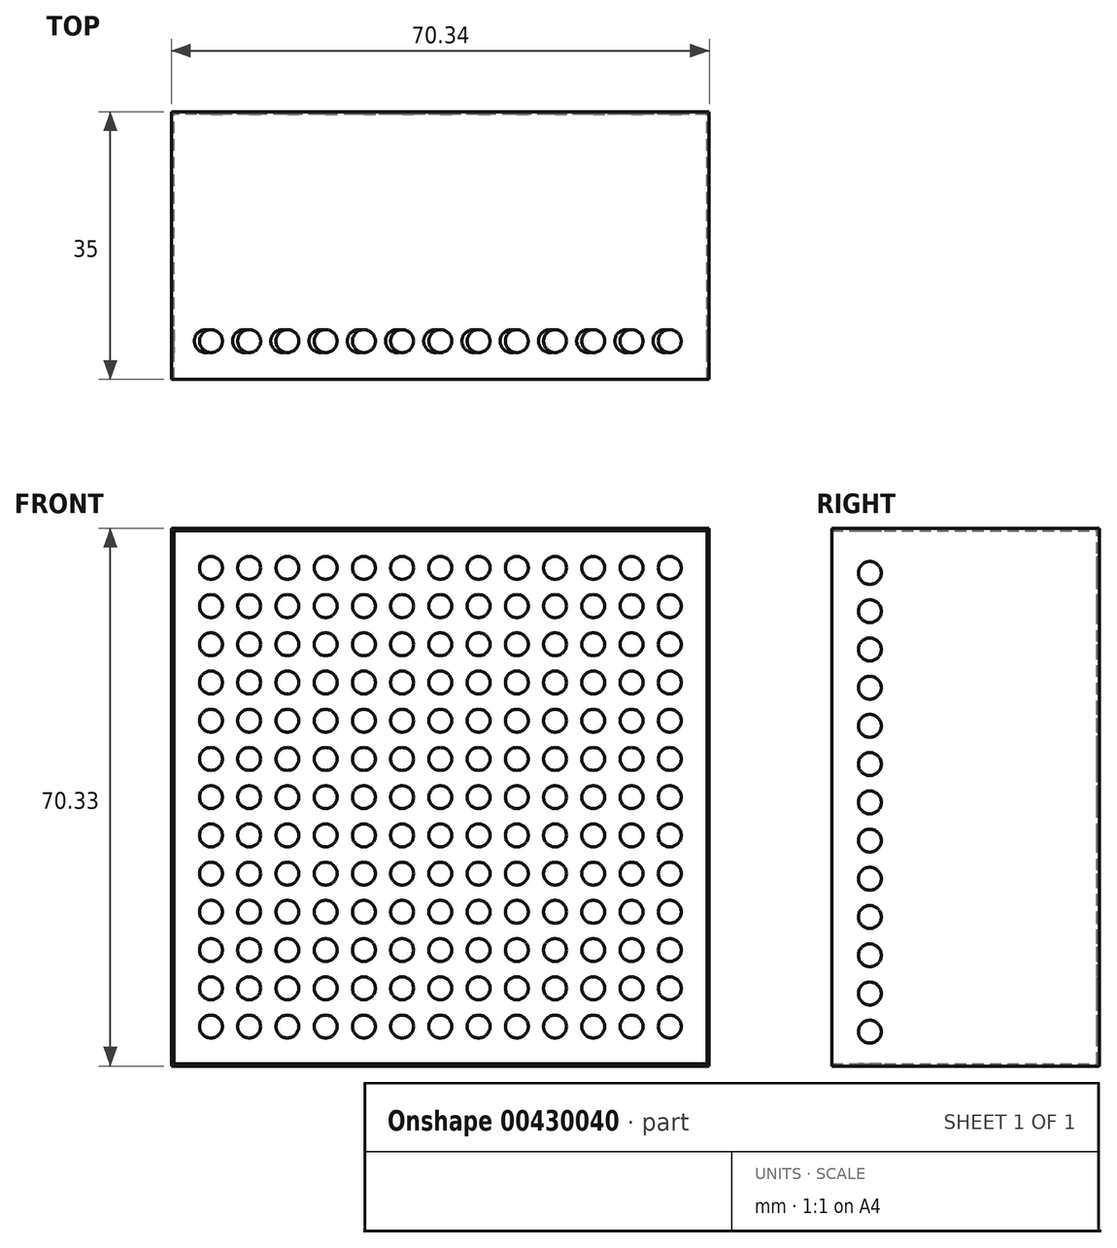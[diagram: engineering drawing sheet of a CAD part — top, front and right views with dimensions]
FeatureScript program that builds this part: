
annotation { "Feature Type Name" : "Feature", "Feature Type Description" : "" }
export const myFeature = defineFeature(function(context is Context, id is Id, definition is map)
    precondition{}
    {
        {
            var Q0;
            Q0=qCreatedBy(makeId("Front.planeOp"),FACE);
            var sketch = newSketch(context, id + "F0", { "sketchPlane" : qUnion([Q0])});
            skLineSegment(sketch, "E0.bottom", {"start": v(35.16, -35.16) * mm, "end": v(-35.16, -35.17) * mm});
            skLineSegment(sketch, "E0.top", {"start": v(35.16, 35.16) * mm, "end": v(-35.16, 35.16) * mm});
            skLineSegment(sketch, "E0.left", {"start": v(35.16, -35.16) * mm, "end": v(35.16, 35.16) * mm});
            skLineSegment(sketch, "E0.right", {"start": v(-35.16, -35.17) * mm, "end": v(-35.16, 35.16) * mm});
            skPoint(sketch, "E0.middle", {"position": v(0, 0) * mm});
            skLineSegment(sketch, "E1", {"start": v(0, 50.16) * mm, "end": v(0, -40.93) * mm, "construction": true});
            skPoint(sketch, "E1.endSnap0", {"position": v(0, 35.16) * mm});
            skLineSegment(sketch, "E2", {"start": v(-54.3, 0) * mm, "end": v(79.67, 0) * mm, "construction": true});
            skPoint(sketch, "E3", {"position": v(-30, 30) * mm});
            skPoint(sketch, "E4.1.0.0", {"position": v(-25, 30) * mm});
            skPoint(sketch, "E4.2.0.0", {"position": v(-20, 30) * mm});
            skPoint(sketch, "E4.3.0.0", {"position": v(-15, 30) * mm});
            skPoint(sketch, "E4.4.0.0", {"position": v(-10, 30) * mm});
            skPoint(sketch, "E4.5.0.0", {"position": v(-5, 30) * mm});
            skPoint(sketch, "E4.6.0.0", {"position": v(0, 30) * mm});
            skPoint(sketch, "E4.7.0.0", {"position": v(5, 30) * mm});
            skPoint(sketch, "E4.8.0.0", {"position": v(10, 30) * mm});
            skPoint(sketch, "E4.9.0.0", {"position": v(15, 30) * mm});
            skPoint(sketch, "E4.10.0.0", {"position": v(20, 30) * mm});
            skPoint(sketch, "E4.11.0.0", {"position": v(25, 30) * mm});
            skPoint(sketch, "E4.12.0.0", {"position": v(30, 30) * mm});
            skLineSegment(sketch, "E4.direction1", {"start": v(-30, 30) * mm, "end": v(-25, 30) * mm, "construction": true});
            skLineSegment(sketch, "E5", {"start": v(-44.02, 27.5) * mm, "end": v(49.73, 27.5) * mm, "construction": true});
            skLineSegment(sketch, "E6", {"start": v(-45.28, 22.5) * mm, "end": v(51.67, 22.5) * mm, "construction": true});
            skLineSegment(sketch, "E7", {"start": v(-45.19, 17.5) * mm, "end": v(53.22, 17.5) * mm, "construction": true});
            skPoint(sketch, "E8.MirrorP", {"position": v(-30, 25) * mm});
            skPoint(sketch, "E9.MirrorP", {"position": v(-25, 25) * mm});
            skPoint(sketch, "E10.MirrorP", {"position": v(-20, 25) * mm});
            skPoint(sketch, "E11.MirrorP", {"position": v(-15, 25) * mm});
            skPoint(sketch, "E12.MirrorP", {"position": v(-10, 25) * mm});
            skPoint(sketch, "E13.MirrorP", {"position": v(-5, 25) * mm});
            skPoint(sketch, "E14.MirrorP", {"position": v(0, 25) * mm});
            skPoint(sketch, "E15.MirrorP", {"position": v(5, 25) * mm});
            skPoint(sketch, "E16.MirrorP", {"position": v(10, 25) * mm});
            skPoint(sketch, "E17.MirrorP", {"position": v(15, 25) * mm});
            skPoint(sketch, "E18.MirrorP", {"position": v(20, 25) * mm});
            skPoint(sketch, "E19.MirrorP", {"position": v(25, 25) * mm});
            skPoint(sketch, "E20.MirrorP", {"position": v(30, 25) * mm});
            skPoint(sketch, "E21.MirrorP", {"position": v(-30, 20) * mm});
            skPoint(sketch, "E22.MirrorP", {"position": v(-25, 20) * mm});
            skPoint(sketch, "E23.MirrorP", {"position": v(-20, 20) * mm});
            skPoint(sketch, "E24.MirrorP", {"position": v(-15, 20) * mm});
            skPoint(sketch, "E25.MirrorP", {"position": v(-10, 20) * mm});
            skPoint(sketch, "E26.MirrorP", {"position": v(-5, 20) * mm});
            skPoint(sketch, "E27.MirrorP", {"position": v(0, 20) * mm});
            skPoint(sketch, "E28.MirrorP", {"position": v(5, 20) * mm});
            skPoint(sketch, "E29.MirrorP", {"position": v(10, 20) * mm});
            skPoint(sketch, "E30.MirrorP", {"position": v(15, 20) * mm});
            skPoint(sketch, "E31.MirrorP", {"position": v(20, 20) * mm});
            skPoint(sketch, "E32.MirrorP", {"position": v(25, 20) * mm});
            skPoint(sketch, "E33.MirrorP", {"position": v(30, 20) * mm});
            skPoint(sketch, "E34.MirrorP", {"position": v(-30, 15) * mm});
            skPoint(sketch, "E35.MirrorP", {"position": v(-25, 15) * mm});
            skPoint(sketch, "E36.MirrorP", {"position": v(-20, 15) * mm});
            skPoint(sketch, "E37.MirrorP", {"position": v(-15, 15) * mm});
            skPoint(sketch, "E38.MirrorP", {"position": v(-10, 15) * mm});
            skPoint(sketch, "E39.MirrorP", {"position": v(-5, 15) * mm});
            skPoint(sketch, "E40.MirrorP", {"position": v(0, 15) * mm});
            skPoint(sketch, "E41.MirrorP", {"position": v(10, 15) * mm});
            skPoint(sketch, "E42.MirrorP", {"position": v(20, 15) * mm});
            skPoint(sketch, "E43.MirrorP", {"position": v(5, 15) * mm});
            skPoint(sketch, "E44.MirrorP", {"position": v(25, 15) * mm});
            skPoint(sketch, "E45.MirrorP", {"position": v(15, 15) * mm});
            skPoint(sketch, "E46.MirrorP", {"position": v(30, 15) * mm});
            skLineSegment(sketch, "E47", {"start": v(-45.96, 12.5) * mm, "end": v(53.42, 12.5) * mm, "construction": true});
            skLineSegment(sketch, "E48", {"start": v(-45.28, 7.5) * mm, "end": v(54.1, 7.5) * mm, "construction": true});
            skLineSegment(sketch, "E49", {"start": v(-42.28, 2.5) * mm, "end": v(50.9, 2.5) * mm, "construction": true});
            skPoint(sketch, "E50.MirrorP", {"position": v(-30, 10) * mm});
            skPoint(sketch, "E51.MirrorP", {"position": v(-25, 10) * mm});
            skPoint(sketch, "E52.MirrorP", {"position": v(-20, 10) * mm});
            skPoint(sketch, "E53.MirrorP", {"position": v(-15, 10) * mm});
            skPoint(sketch, "E54.MirrorP", {"position": v(-10, 10) * mm});
            skPoint(sketch, "E55.MirrorP", {"position": v(-5, 10) * mm});
            skPoint(sketch, "E56.MirrorP", {"position": v(0, 10) * mm});
            skPoint(sketch, "E57.MirrorP", {"position": v(5, 10) * mm});
            skPoint(sketch, "E58.MirrorP", {"position": v(10, 10) * mm});
            skPoint(sketch, "E59.MirrorP", {"position": v(15, 10) * mm});
            skPoint(sketch, "E60.MirrorP", {"position": v(20, 10) * mm});
            skPoint(sketch, "E61.MirrorP", {"position": v(30, 10) * mm});
            skPoint(sketch, "E62.MirrorP", {"position": v(25, 10) * mm});
            skPoint(sketch, "E63.MirrorP", {"position": v(-30, 5) * mm});
            skPoint(sketch, "E64.MirrorP", {"position": v(-25, 5) * mm});
            skPoint(sketch, "E65.MirrorP", {"position": v(15, 5) * mm});
            skPoint(sketch, "E66.MirrorP", {"position": v(-15, 5) * mm});
            skPoint(sketch, "E67.MirrorP", {"position": v(-20, 5) * mm});
            skPoint(sketch, "E68.MirrorP", {"position": v(30, 5) * mm});
            skPoint(sketch, "E69.MirrorP", {"position": v(-5, 5) * mm});
            skPoint(sketch, "E70.MirrorP", {"position": v(20, 5) * mm});
            skPoint(sketch, "E71.MirrorP", {"position": v(-10, 5) * mm});
            skPoint(sketch, "E72.MirrorP", {"position": v(10, 5) * mm});
            skPoint(sketch, "E73.MirrorP", {"position": v(5, 5) * mm});
            skPoint(sketch, "E74.MirrorP", {"position": v(25, 5) * mm});
            skPoint(sketch, "E75.MirrorP", {"position": v(0, 5) * mm});
            skPoint(sketch, "E76.MirrorP", {"position": v(30, 0) * mm});
            skPoint(sketch, "E77.MirrorP", {"position": v(5, 0) * mm});
            skPoint(sketch, "E78.MirrorP", {"position": v(10, 0) * mm});
            skPoint(sketch, "E79.MirrorP", {"position": v(15, 0) * mm});
            skPoint(sketch, "E80.MirrorP", {"position": v(-5, 0) * mm});
            skPoint(sketch, "E81.MirrorP", {"position": v(-10, 0) * mm});
            skPoint(sketch, "E82.MirrorP", {"position": v(-25, 0) * mm});
            skPoint(sketch, "E83.MirrorP", {"position": v(-15, 0) * mm});
            skPoint(sketch, "E84.MirrorP", {"position": v(20, 0) * mm});
            skPoint(sketch, "E85.MirrorP", {"position": v(-20, 0) * mm});
            skPoint(sketch, "E86.MirrorP", {"position": v(-30, 0) * mm});
            skPoint(sketch, "E87.MirrorP", {"position": v(25, 0) * mm});
            skPoint(sketch, "E88.MirrorP", {"position": v(-15, -20) * mm});
            skPoint(sketch, "E89.MirrorP", {"position": v(0, -15) * mm});
            skPoint(sketch, "E90.MirrorP", {"position": v(15, -10) * mm});
            skPoint(sketch, "E91.MirrorP", {"position": v(0, -5) * mm});
            skPoint(sketch, "E92.MirrorP", {"position": v(-30, -25) * mm});
            skPoint(sketch, "E93.MirrorP", {"position": v(-20, -10) * mm});
            skPoint(sketch, "E94.MirrorP", {"position": v(30, -5) * mm});
            skPoint(sketch, "E95.MirrorP", {"position": v(0, -30) * mm});
            skPoint(sketch, "E96.MirrorP", {"position": v(15, -25) * mm});
            skPoint(sketch, "E97.MirrorP", {"position": v(30, -20) * mm});
            skPoint(sketch, "E98.MirrorP", {"position": v(-30, -15) * mm});
            skPoint(sketch, "E99.MirrorP", {"position": v(20, -25) * mm});
            skPoint(sketch, "E100.MirrorP", {"position": v(5, -30) * mm});
            skPoint(sketch, "E101.MirrorP", {"position": v(-5, -5) * mm});
            skPoint(sketch, "E102.MirrorP", {"position": v(-15, -10) * mm});
            skPoint(sketch, "E103.MirrorP", {"position": v(-25, -25) * mm});
            skPoint(sketch, "E104.MirrorP", {"position": v(20, -10) * mm});
            skPoint(sketch, "E105.MirrorP", {"position": v(0, -10) * mm});
            skPoint(sketch, "E106.MirrorP", {"position": v(30, -15) * mm});
            skPoint(sketch, "E107.MirrorP", {"position": v(10, -15) * mm});
            skPoint(sketch, "E108.MirrorP", {"position": v(10, -5) * mm});
            skPoint(sketch, "E109.MirrorP", {"position": v(-10, -20) * mm});
            skPoint(sketch, "E110.MirrorP", {"position": v(15, -5) * mm});
            skPoint(sketch, "E111.MirrorP", {"position": v(-15, -5) * mm});
            skPoint(sketch, "E112.MirrorP", {"position": v(-30, -10) * mm});
            skPoint(sketch, "E113.MirrorP", {"position": v(20, -30) * mm});
            skPoint(sketch, "E114.MirrorP", {"position": v(-20, -25) * mm});
            skLineSegment(sketch, "E115.MirrorCS", {"start": v(-30, -30) * mm, "end": v(-25, -30) * mm, "construction": true});
            skPoint(sketch, "E116.MirrorP", {"position": v(30, -10) * mm});
            skPoint(sketch, "E117.MirrorP", {"position": v(-10, -30) * mm});
            skPoint(sketch, "E118.MirrorP", {"position": v(5, -25) * mm});
            skPoint(sketch, "E119.MirrorP", {"position": v(20, -15) * mm});
            skPoint(sketch, "E120.MirrorP", {"position": v(-5, -20) * mm});
            skPoint(sketch, "E121.MirrorP", {"position": v(15, -15) * mm});
            skPoint(sketch, "E122.MirrorP", {"position": v(-25, -5) * mm});
            skPoint(sketch, "E123.MirrorP", {"position": v(25, -25) * mm});
            skPoint(sketch, "E124.MirrorP", {"position": v(-25, -30) * mm});
            skPoint(sketch, "E125.MirrorP", {"position": v(5, -15) * mm});
            skPoint(sketch, "E126.MirrorP", {"position": v(-15, -25) * mm});
            skPoint(sketch, "E127.MirrorP", {"position": v(30, -25) * mm});
            skPoint(sketch, "E128.MirrorP", {"position": v(15, -30) * mm});
            skPoint(sketch, "E129.MirrorP", {"position": v(-25, -10) * mm});
            skPoint(sketch, "E130.MirrorP", {"position": v(-5, -10) * mm});
            skPoint(sketch, "E131.MirrorP", {"position": v(25, -15) * mm});
            skPoint(sketch, "E132.MirrorP", {"position": v(-10, -10) * mm});
            skPoint(sketch, "E133.MirrorP", {"position": v(30, -30) * mm});
            skPoint(sketch, "E134.MirrorP", {"position": v(-30, -30) * mm});
            skPoint(sketch, "E135.MirrorP", {"position": v(-10, -5) * mm});
            skPoint(sketch, "E136.MirrorP", {"position": v(20, -5) * mm});
            skPoint(sketch, "E137.MirrorP", {"position": v(0, -20) * mm});
            skPoint(sketch, "E138.MirrorP", {"position": v(-20, -20) * mm});
            skPoint(sketch, "E139.MirrorP", {"position": v(20, -20) * mm});
            skPoint(sketch, "E140.MirrorP", {"position": v(5, -10) * mm});
            skPoint(sketch, "E141.MirrorP", {"position": v(25, -30) * mm});
            skPoint(sketch, "E142.MirrorP", {"position": v(5, -5) * mm});
            skPoint(sketch, "E143.MirrorP", {"position": v(10, -30) * mm});
            skPoint(sketch, "E144.MirrorP", {"position": v(25, -5) * mm});
            skPoint(sketch, "E145.MirrorP", {"position": v(-20, -30) * mm});
            skPoint(sketch, "E146.MirrorP", {"position": v(25, -10) * mm});
            skPoint(sketch, "E147.MirrorP", {"position": v(15, -20) * mm});
            skPoint(sketch, "E148.MirrorP", {"position": v(-5, -25) * mm});
            skPoint(sketch, "E149.MirrorP", {"position": v(10, -25) * mm});
            skPoint(sketch, "E150.MirrorP", {"position": v(10, -10) * mm});
            skPoint(sketch, "E151.MirrorP", {"position": v(-30, -5) * mm});
            skPoint(sketch, "E152.MirrorP", {"position": v(-5, -15) * mm});
            skPoint(sketch, "E153.MirrorP", {"position": v(-10, -15) * mm});
            skPoint(sketch, "E154.MirrorP", {"position": v(10, -20) * mm});
            skPoint(sketch, "E155.MirrorP", {"position": v(-20, -5) * mm});
            skPoint(sketch, "E156.MirrorP", {"position": v(-5, -30) * mm});
            skPoint(sketch, "E157.MirrorP", {"position": v(5, -20) * mm});
            skPoint(sketch, "E158.MirrorP", {"position": v(-25, -15) * mm});
            skPoint(sketch, "E159.MirrorP", {"position": v(-30, -20) * mm});
            skPoint(sketch, "E160.MirrorP", {"position": v(-15, -30) * mm});
            skPoint(sketch, "E161.MirrorP", {"position": v(25, -20) * mm});
            skPoint(sketch, "E162.MirrorP", {"position": v(-10, -25) * mm});
            skPoint(sketch, "E163.MirrorP", {"position": v(-15, -15) * mm});
            skPoint(sketch, "E164.MirrorP", {"position": v(-20, -15) * mm});
            skPoint(sketch, "E165.MirrorP", {"position": v(0, -25) * mm});
            skPoint(sketch, "E166.MirrorP", {"position": v(-25, -20) * mm});
            skSolve(sketch);
        }
        {
            var Q0;
            Q0=makeQuery(id+"F0.imprint","IMPRINT",FACE,{"disambiguationData":[TD([[makeQuery(id+"F0.imprint","IMPRINT",EDGE,{"derivedFrom":sQuery(id+"F0.wireOp",EDGE,"E0.bottom")}),-1.0]])]});
            extrude(context, id + "F1", {"entities" : qUnion([Q0]), "depth" : 35 * mm});
        }
        {
            var Q0;
            Q0=makeQuery(id+"F1.opExtrude","CAP_FACE",FACE,{"disambiguationData":[OSD([sQuery(id+"F0.wireOp",EDGE,"E0.bottom"),sQuery(id+"F0.wireOp",EDGE,"E0.top"),sQuery(id+"F0.wireOp",EDGE,"E0.left"),sQuery(id+"F0.wireOp",EDGE,"E0.right")])],"isStart":false});
            shell(context, id + "F2", {"entities" : qUnion([Q0]), "thickness" : 0.3 * mm});
        }
        {
            var Q0;
            Q0=sQuery(id+"F0.wireOp",VERTEX,"E4.12.0.0");
            var Q1;
            Q1=sQuery(id+"F0.wireOp",VERTEX,"E42.MirrorP");
            var Q2;
            Q2=sQuery(id+"F0.wireOp",VERTEX,"E29.MirrorP");
            var Q3;
            Q3=sQuery(id+"F0.wireOp",VERTEX,"E17.MirrorP");
            var Q4;
            Q4=sQuery(id+"F0.wireOp",VERTEX,"E30.MirrorP");
            var Q5;
            Q5=sQuery(id+"F0.wireOp",VERTEX,"E4.9.0.0");
            var Q6;
            Q6=sQuery(id+"F0.wireOp",VERTEX,"E4.7.0.0");
            var Q7;
            Q7=sQuery(id+"F0.wireOp",VERTEX,"E43.MirrorP");
            var Q8;
            Q8=sQuery(id+"F0.wireOp",VERTEX,"E18.MirrorP");
            var Q9;
            Q9=sQuery(id+"F0.wireOp",VERTEX,"E41.MirrorP");
            var Q10;
            Q10=sQuery(id+"F0.wireOp",VERTEX,"E4.10.0.0");
            var Q11;
            Q11=sQuery(id+"F0.wireOp",VERTEX,"E45.MirrorP");
            var Q12;
            Q12=sQuery(id+"F0.wireOp",VERTEX,"E16.MirrorP");
            var Q13;
            Q13=sQuery(id+"F0.wireOp",VERTEX,"E32.MirrorP");
            var Q14;
            Q14=sQuery(id+"F0.wireOp",VERTEX,"E28.MirrorP");
            var Q15;
            Q15=sQuery(id+"F0.wireOp",VERTEX,"E19.MirrorP");
            var Q16;
            Q16=sQuery(id+"F0.wireOp",VERTEX,"E4.8.0.0");
            var Q17;
            Q17=sQuery(id+"F0.wireOp",VERTEX,"E44.MirrorP");
            var Q18;
            Q18=sQuery(id+"F0.wireOp",VERTEX,"E31.MirrorP");
            var Q19;
            Q19=sQuery(id+"F0.wireOp",VERTEX,"E15.MirrorP");
            var Q20;
            Q20=sQuery(id+"F0.wireOp",VERTEX,"E4.11.0.0");
            var Q21;
            Q21=sQuery(id+"F0.wireOp",VERTEX,"E33.MirrorP");
            var Q22;
            Q22=sQuery(id+"F0.wireOp",VERTEX,"E46.MirrorP");
            var Q23;
            Q23=sQuery(id+"F0.wireOp",VERTEX,"E68.MirrorP");
            var Q24;
            Q24=sQuery(id+"F0.wireOp",VERTEX,"E61.MirrorP");
            var Q25;
            Q25=sQuery(id+"F0.wireOp",VERTEX,"E76.MirrorP");
            var Q26;
            Q26=sQuery(id+"F0.wireOp",VERTEX,"E20.MirrorP");
            var Q27;
            Q27=sQuery(id+"F0.wireOp",VERTEX,"E106.MirrorP");
            var Q28;
            Q28=sQuery(id+"F0.wireOp",VERTEX,"E116.MirrorP");
            var Q29;
            Q29=sQuery(id+"F0.wireOp",VERTEX,"E94.MirrorP");
            var Q30;
            Q30=sQuery(id+"F0.wireOp",VERTEX,"E127.MirrorP");
            var Q31;
            Q31=sQuery(id+"F0.wireOp",VERTEX,"E97.MirrorP");
            var Q32;
            Q32=sQuery(id+"F0.wireOp",VERTEX,"E149.MirrorP");
            var Q33;
            Q33=sQuery(id+"F0.wireOp",VERTEX,"E96.MirrorP");
            var Q34;
            Q34=sQuery(id+"F0.wireOp",VERTEX,"E142.MirrorP");
            var Q35;
            Q35=sQuery(id+"F0.wireOp",VERTEX,"E157.MirrorP");
            var Q36;
            Q36=sQuery(id+"F0.wireOp",VERTEX,"E62.MirrorP");
            var Q37;
            Q37=sQuery(id+"F0.wireOp",VERTEX,"E74.MirrorP");
            var Q38;
            Q38=sQuery(id+"F0.wireOp",VERTEX,"E131.MirrorP");
            var Q39;
            Q39=sQuery(id+"F0.wireOp",VERTEX,"E161.MirrorP");
            var Q40;
            Q40=sQuery(id+"F0.wireOp",VERTEX,"E147.MirrorP");
            var Q41;
            Q41=sQuery(id+"F0.wireOp",VERTEX,"E65.MirrorP");
            var Q42;
            Q42=sQuery(id+"F0.wireOp",VERTEX,"E77.MirrorP");
            var Q43;
            Q43=sQuery(id+"F0.wireOp",VERTEX,"E100.MirrorP");
            var Q44;
            Q44=sQuery(id+"F0.wireOp",VERTEX,"E99.MirrorP");
            var Q45;
            Q45=sQuery(id+"F0.wireOp",VERTEX,"E84.MirrorP");
            var Q46;
            Q46=sQuery(id+"F0.wireOp",VERTEX,"E90.MirrorP");
            var Q47;
            Q47=sQuery(id+"F0.wireOp",VERTEX,"E139.MirrorP");
            var Q48;
            Q48=sQuery(id+"F0.wireOp",VERTEX,"E123.MirrorP");
            var Q49;
            Q49=sQuery(id+"F0.wireOp",VERTEX,"E60.MirrorP");
            var Q50;
            Q50=sQuery(id+"F0.wireOp",VERTEX,"E140.MirrorP");
            var Q51;
            Q51=sQuery(id+"F0.wireOp",VERTEX,"E107.MirrorP");
            var Q52;
            Q52=sQuery(id+"F0.wireOp",VERTEX,"E72.MirrorP");
            var Q53;
            Q53=sQuery(id+"F0.wireOp",VERTEX,"E59.MirrorP");
            var Q54;
            Q54=sQuery(id+"F0.wireOp",VERTEX,"E128.MirrorP");
            var Q55;
            Q55=sQuery(id+"F0.wireOp",VERTEX,"E144.MirrorP");
            var Q56;
            Q56=sQuery(id+"F0.wireOp",VERTEX,"E79.MirrorP");
            var Q57;
            Q57=sQuery(id+"F0.wireOp",VERTEX,"E119.MirrorP");
            var Q58;
            Q58=sQuery(id+"F0.wireOp",VERTEX,"E108.MirrorP");
            var Q59;
            Q59=sQuery(id+"F0.wireOp",VERTEX,"E125.MirrorP");
            var Q60;
            Q60=sQuery(id+"F0.wireOp",VERTEX,"E141.MirrorP");
            var Q61;
            Q61=sQuery(id+"F0.wireOp",VERTEX,"E154.MirrorP");
            var Q62;
            Q62=sQuery(id+"F0.wireOp",VERTEX,"E58.MirrorP");
            var Q63;
            Q63=sQuery(id+"F0.wireOp",VERTEX,"E136.MirrorP");
            var Q64;
            Q64=sQuery(id+"F0.wireOp",VERTEX,"E87.MirrorP");
            var Q65;
            Q65=sQuery(id+"F0.wireOp",VERTEX,"E78.MirrorP");
            var Q66;
            Q66=sQuery(id+"F0.wireOp",VERTEX,"E70.MirrorP");
            var Q67;
            Q67=sQuery(id+"F0.wireOp",VERTEX,"E143.MirrorP");
            var Q68;
            Q68=sQuery(id+"F0.wireOp",VERTEX,"E150.MirrorP");
            var Q69;
            Q69=sQuery(id+"F0.wireOp",VERTEX,"E118.MirrorP");
            var Q70;
            Q70=sQuery(id+"F0.wireOp",VERTEX,"E110.MirrorP");
            var Q71;
            Q71=sQuery(id+"F0.wireOp",VERTEX,"E146.MirrorP");
            var Q72;
            Q72=sQuery(id+"F0.wireOp",VERTEX,"E113.MirrorP");
            var Q73;
            Q73=sQuery(id+"F0.wireOp",VERTEX,"E73.MirrorP");
            var Q74;
            Q74=sQuery(id+"F0.wireOp",VERTEX,"E57.MirrorP");
            var Q75;
            Q75=sQuery(id+"F0.wireOp",VERTEX,"E121.MirrorP");
            var Q76;
            Q76=sQuery(id+"F0.wireOp",VERTEX,"E104.MirrorP");
            var Q77;
            Q77=sQuery(id+"F0.wireOp",VERTEX,"E89.MirrorP");
            var Q78;
            Q78=sQuery(id+"F0.wireOp",VERTEX,"E133.MirrorP");
            var Q79;
            Q79=sQuery(id+"F0.wireOp",VERTEX,"E158.MirrorP");
            var Q80;
            Q80=sQuery(id+"F0.wireOp",VERTEX,"E164.MirrorP");
            var Q81;
            Q81=sQuery(id+"F0.wireOp",VERTEX,"E152.MirrorP");
            var Q82;
            Q82=sQuery(id+"F0.wireOp",VERTEX,"E98.MirrorP");
            var Q83;
            Q83=sQuery(id+"F0.wireOp",VERTEX,"E163.MirrorP");
            var Q84;
            Q84=sQuery(id+"F0.wireOp",VERTEX,"E153.MirrorP");
            var Q85;
            Q85=sQuery(id+"F0.wireOp",VERTEX,"E109.MirrorP");
            var Q86;
            Q86=sQuery(id+"F0.wireOp",VERTEX,"E138.MirrorP");
            var Q87;
            Q87=sQuery(id+"F0.wireOp",VERTEX,"E120.MirrorP");
            var Q88;
            Q88=sQuery(id+"F0.wireOp",VERTEX,"E166.MirrorP");
            var Q89;
            Q89=sQuery(id+"F0.wireOp",VERTEX,"E159.MirrorP");
            var Q90;
            Q90=sQuery(id+"F0.wireOp",VERTEX,"E137.MirrorP");
            var Q91;
            Q91=sQuery(id+"F0.wireOp",VERTEX,"E88.MirrorP");
            var Q92;
            Q92=sQuery(id+"F0.wireOp",VERTEX,"E165.MirrorP");
            var Q93;
            Q93=sQuery(id+"F0.wireOp",VERTEX,"E114.MirrorP");
            var Q94;
            Q94=sQuery(id+"F0.wireOp",VERTEX,"E126.MirrorP");
            var Q95;
            Q95=sQuery(id+"F0.wireOp",VERTEX,"E92.MirrorP");
            var Q96;
            Q96=sQuery(id+"F0.wireOp",VERTEX,"E148.MirrorP");
            var Q97;
            Q97=sQuery(id+"F0.wireOp",VERTEX,"E103.MirrorP");
            var Q98;
            Q98=sQuery(id+"F0.wireOp",VERTEX,"E162.MirrorP");
            var Q99;
            Q99=makeQuery(id+"F1.opExtrude","SWEPT_BODY",BODY,{"disambiguationData":[OSD([sQuery(id+"F0.wireOp",EDGE,"E0.bottom"),sQuery(id+"F0.wireOp",EDGE,"E0.top"),sQuery(id+"F0.wireOp",EDGE,"E0.left"),sQuery(id+"F0.wireOp",EDGE,"E0.right")])]});
            hole(context, id + "F3", {"style" : HoleStyle.SIMPLE, "endStyle" : HoleEndStyle.BLIND, "oppositeDirection" : true, "holeDiameter" : 3 * mm, "holeDepth" : 1 * mm, "tappedDepth" : 12 * mm, "tapClearance" : 3, "locations" : qUnion([Q0, Q1, Q2, Q3, Q4, Q5, Q6, Q7, Q8, Q9, Q10, Q11, Q12, Q13, Q14, Q15, Q16, Q17, Q18, Q19, Q20, Q21, Q22, Q23, Q24, Q25, Q26, Q27, Q28, Q29, Q30, Q31, Q32, Q33, Q34, Q35, Q36, Q37, Q38, Q39, Q40, Q41, Q42, Q43, Q44, Q45, Q46, Q47, Q48, Q49, Q50, Q51, Q52, Q53, Q54, Q55, Q56, Q57, Q58, Q59, Q60, Q61, Q62, Q63, Q64, Q65, Q66, Q67, Q68, Q69, Q70, Q71, Q72, Q73, Q74, Q75, Q76, Q77, Q78, Q79, Q80, Q81, Q82, Q83, Q84, Q85, Q86, Q87, Q88, Q89, Q90, Q91, Q92, Q93, Q94, Q95, Q96, Q97, Q98]), "scope" : qUnion([Q99])});
        }
        {
            var Q0;
            Q0=sQuery(id+"F0.wireOp",VERTEX,"E4.3.0.0");
            var Q1;
            Q1=sQuery(id+"F0.wireOp",VERTEX,"E4.2.0.0");
            var Q2;
            Q2=sQuery(id+"F0.wireOp",VERTEX,"E4.6.0.0");
            var Q3;
            Q3=sQuery(id+"F0.wireOp",VERTEX,"E3");
            var Q4;
            Q4=sQuery(id+"F0.wireOp",VERTEX,"E4.5.0.0");
            var Q5;
            Q5=sQuery(id+"F0.wireOp",VERTEX,"E4.1.0.0");
            var Q6;
            Q6=sQuery(id+"F0.wireOp",VERTEX,"E4.4.0.0");
            var Q7;
            Q7=sQuery(id+"F0.wireOp",VERTEX,"E14.MirrorP");
            var Q8;
            Q8=sQuery(id+"F0.wireOp",VERTEX,"E9.MirrorP");
            var Q9;
            Q9=sQuery(id+"F0.wireOp",VERTEX,"E13.MirrorP");
            var Q10;
            Q10=sQuery(id+"F0.wireOp",VERTEX,"E10.MirrorP");
            var Q11;
            Q11=sQuery(id+"F0.wireOp",VERTEX,"E11.MirrorP");
            var Q12;
            Q12=sQuery(id+"F0.wireOp",VERTEX,"E8.MirrorP");
            var Q13;
            Q13=sQuery(id+"F0.wireOp",VERTEX,"E12.MirrorP");
            var Q14;
            Q14=sQuery(id+"F0.wireOp",VERTEX,"E26.MirrorP");
            var Q15;
            Q15=sQuery(id+"F0.wireOp",VERTEX,"E27.MirrorP");
            var Q16;
            Q16=sQuery(id+"F0.wireOp",VERTEX,"E24.MirrorP");
            var Q17;
            Q17=sQuery(id+"F0.wireOp",VERTEX,"E25.MirrorP");
            var Q18;
            Q18=sQuery(id+"F0.wireOp",VERTEX,"E23.MirrorP");
            var Q19;
            Q19=sQuery(id+"F0.wireOp",VERTEX,"E21.MirrorP");
            var Q20;
            Q20=sQuery(id+"F0.wireOp",VERTEX,"E22.MirrorP");
            var Q21;
            Q21=sQuery(id+"F0.wireOp",VERTEX,"E36.MirrorP");
            var Q22;
            Q22=sQuery(id+"F0.wireOp",VERTEX,"E34.MirrorP");
            var Q23;
            Q23=sQuery(id+"F0.wireOp",VERTEX,"E40.MirrorP");
            var Q24;
            Q24=sQuery(id+"F0.wireOp",VERTEX,"E39.MirrorP");
            var Q25;
            Q25=sQuery(id+"F0.wireOp",VERTEX,"E37.MirrorP");
            var Q26;
            Q26=sQuery(id+"F0.wireOp",VERTEX,"E35.MirrorP");
            var Q27;
            Q27=sQuery(id+"F0.wireOp",VERTEX,"E38.MirrorP");
            var Q28;
            Q28=sQuery(id+"F0.wireOp",VERTEX,"E53.MirrorP");
            var Q29;
            Q29=sQuery(id+"F0.wireOp",VERTEX,"E52.MirrorP");
            var Q30;
            Q30=sQuery(id+"F0.wireOp",VERTEX,"E51.MirrorP");
            var Q31;
            Q31=sQuery(id+"F0.wireOp",VERTEX,"E55.MirrorP");
            var Q32;
            Q32=sQuery(id+"F0.wireOp",VERTEX,"E56.MirrorP");
            var Q33;
            Q33=sQuery(id+"F0.wireOp",VERTEX,"E54.MirrorP");
            var Q34;
            Q34=sQuery(id+"F0.wireOp",VERTEX,"E50.MirrorP");
            var Q35;
            Q35=sQuery(id+"F0.wireOp",VERTEX,"E69.MirrorP");
            var Q36;
            Q36=sQuery(id+"F0.wireOp",VERTEX,"E67.MirrorP");
            var Q37;
            Q37=sQuery(id+"F0.wireOp",VERTEX,"E71.MirrorP");
            var Q38;
            Q38=sQuery(id+"F0.wireOp",VERTEX,"E75.MirrorP");
            var Q39;
            Q39=sQuery(id+"F0.wireOp",VERTEX,"E64.MirrorP");
            var Q40;
            Q40=sQuery(id+"F0.wireOp",VERTEX,"E63.MirrorP");
            var Q41;
            Q41=sQuery(id+"F0.wireOp",VERTEX,"E66.MirrorP");
            var Q42;
            Q42=sQuery(id+"F0.wireOp",VERTEX,"E80.MirrorP");
            var Q43;
            Q43=sQuery(id+"F0.wireOp",VERTEX,"E82.MirrorP");
            var Q44;
            Q44=sQuery(id+"F0.wireOp",VERTEX,"E83.MirrorP");
            var Q45;
            Q45=sQuery(id+"F0.wireOp",VERTEX,"E0.middle");
            var Q46;
            Q46=sQuery(id+"F0.wireOp",VERTEX,"E86.MirrorP");
            var Q47;
            Q47=sQuery(id+"F0.wireOp",VERTEX,"E85.MirrorP");
            var Q48;
            Q48=sQuery(id+"F0.wireOp",VERTEX,"E81.MirrorP");
            var Q49;
            Q49=sQuery(id+"F0.wireOp",VERTEX,"E112.MirrorP");
            var Q50;
            Q50=sQuery(id+"F0.wireOp",VERTEX,"E129.MirrorP");
            var Q51;
            Q51=sQuery(id+"F0.wireOp",VERTEX,"E93.MirrorP");
            var Q52;
            Q52=sQuery(id+"F0.wireOp",VERTEX,"E155.MirrorP");
            var Q53;
            Q53=sQuery(id+"F0.wireOp",VERTEX,"E91.MirrorP");
            var Q54;
            Q54=sQuery(id+"F0.wireOp",VERTEX,"E111.MirrorP");
            var Q55;
            Q55=sQuery(id+"F0.wireOp",VERTEX,"E151.MirrorP");
            var Q56;
            Q56=sQuery(id+"F0.wireOp",VERTEX,"E102.MirrorP");
            var Q57;
            Q57=sQuery(id+"F0.wireOp",VERTEX,"E135.MirrorP");
            var Q58;
            Q58=sQuery(id+"F0.wireOp",VERTEX,"E132.MirrorP");
            var Q59;
            Q59=sQuery(id+"F0.wireOp",VERTEX,"E105.MirrorP");
            var Q60;
            Q60=sQuery(id+"F0.wireOp",VERTEX,"E122.MirrorP");
            var Q61;
            Q61=sQuery(id+"F0.wireOp",VERTEX,"E101.MirrorP");
            var Q62;
            Q62=sQuery(id+"F0.wireOp",VERTEX,"E130.MirrorP");
            var Q63;
            Q63=sQuery(id+"F0.wireOp",VERTEX,"E145.MirrorP");
            var Q64;
            Q64=sQuery(id+"F0.wireOp",VERTEX,"E117.MirrorP");
            var Q65;
            Q65=sQuery(id+"F0.wireOp",VERTEX,"E124.MirrorP");
            var Q66;
            Q66=sQuery(id+"F0.wireOp",VERTEX,"E156.MirrorP");
            var Q67;
            Q67=sQuery(id+"F0.wireOp",VERTEX,"E160.MirrorP");
            var Q68;
            Q68=sQuery(id+"F0.wireOp",VERTEX,"E95.MirrorP");
            var Q69;
            Q69=sQuery(id+"F0.wireOp",VERTEX,"E134.MirrorP");
            var Q70;
            Q70=makeQuery(id+"F1.opExtrude","SWEPT_BODY",BODY,{"disambiguationData":[OSD([sQuery(id+"F0.wireOp",EDGE,"E0.bottom"),sQuery(id+"F0.wireOp",EDGE,"E0.top"),sQuery(id+"F0.wireOp",EDGE,"E0.left"),sQuery(id+"F0.wireOp",EDGE,"E0.right")])]});
            hole(context, id + "F4", {"style" : HoleStyle.SIMPLE, "endStyle" : HoleEndStyle.BLIND, "oppositeDirection" : true, "holeDiameter" : 3 * mm, "holeDepth" : 1 * mm, "tappedDepth" : 12 * mm, "tapClearance" : 3, "locations" : qUnion([Q0, Q1, Q2, Q3, Q4, Q5, Q6, Q7, Q8, Q9, Q10, Q11, Q12, Q13, Q14, Q15, Q16, Q17, Q18, Q19, Q20, Q21, Q22, Q23, Q24, Q25, Q26, Q27, Q28, Q29, Q30, Q31, Q32, Q33, Q34, Q35, Q36, Q37, Q38, Q39, Q40, Q41, Q42, Q43, Q44, Q45, Q46, Q47, Q48, Q49, Q50, Q51, Q52, Q53, Q54, Q55, Q56, Q57, Q58, Q59, Q60, Q61, Q62, Q63, Q64, Q65, Q66, Q67, Q68, Q69]), "scope" : qUnion([Q70])});
        }
        {
            var Q0;
            Q0=makeQuery(id+"F1.opExtrude","SWEPT_FACE",FACE,{"disambiguationData":[OSD([sQuery(id+"F0.wireOp",EDGE,"E0.right")])]});
            cPlane(context, id + "F5", {"entities" : qUnion([Q0]), "cplaneType" : CPlaneType.OFFSET, "offset" : 0 * mm, "width" : 150 * mm, "height" : 150 * mm});
        }
        {
            var Q0;
            Q0=qCreatedBy(id+"F5.planeOp",FACE);
            var sketch = newSketch(context, id + "F6", { "sketchPlane" : qUnion([Q0])});
            skLineSegment(sketch, "E167", {"start": v(-3.01, 0) * mm, "end": v(37.2, 0) * mm, "construction": true});
            skPoint(sketch, "E168", {"position": v(30, 29.32) * mm});
            skPoint(sketch, "E169.1.0.0", {"position": v(30, 24.32) * mm});
            skPoint(sketch, "E169.2.0.0", {"position": v(30, 19.32) * mm});
            skPoint(sketch, "E169.3.0.0", {"position": v(30, 14.32) * mm});
            skPoint(sketch, "E169.4.0.0", {"position": v(30, 9.32) * mm});
            skPoint(sketch, "E169.5.0.0", {"position": v(30, 4.32) * mm});
            skPoint(sketch, "E169.6.0.0", {"position": v(30, -0.68) * mm});
            skPoint(sketch, "E169.7.0.0", {"position": v(30, -5.68) * mm});
            skPoint(sketch, "E169.8.0.0", {"position": v(30, -10.68) * mm});
            skPoint(sketch, "E169.9.0.0", {"position": v(30, -15.68) * mm});
            skPoint(sketch, "E169.10.0.0", {"position": v(30, -20.67) * mm});
            skPoint(sketch, "E169.11.0.0", {"position": v(30, -25.68) * mm});
            skPoint(sketch, "E169.12.0.0", {"position": v(30, -30.68) * mm});
            skLineSegment(sketch, "E169.direction1", {"start": v(30, 29.32) * mm, "end": v(30, 24.32) * mm, "construction": true});
            skPoint(sketch, "E170", {"position": v(0, 0) * mm});
            skSolve(sketch);
        }
        {
            var Q0;
            Q0=sQuery(id+"F6.wireOp",VERTEX,"E169.12.0.0");
            var Q1;
            Q1=sQuery(id+"F6.wireOp",VERTEX,"E169.11.0.0");
            var Q2;
            Q2=sQuery(id+"F6.wireOp",VERTEX,"E169.10.0.0");
            var Q3;
            Q3=sQuery(id+"F6.wireOp",VERTEX,"E169.9.0.0");
            var Q4;
            Q4=sQuery(id+"F6.wireOp",VERTEX,"E169.8.0.0");
            var Q5;
            Q5=sQuery(id+"F6.wireOp",VERTEX,"E169.7.0.0");
            var Q6;
            Q6=sQuery(id+"F6.wireOp",VERTEX,"E169.6.0.0");
            var Q7;
            Q7=sQuery(id+"F6.wireOp",VERTEX,"E169.5.0.0");
            var Q8;
            Q8=sQuery(id+"F6.wireOp",VERTEX,"E169.4.0.0");
            var Q9;
            Q9=sQuery(id+"F6.wireOp",VERTEX,"E169.3.0.0");
            var Q10;
            Q10=sQuery(id+"F6.wireOp",VERTEX,"E169.2.0.0");
            var Q11;
            Q11=sQuery(id+"F6.wireOp",VERTEX,"E169.1.0.0");
            var Q12;
            Q12=sQuery(id+"F6.wireOp",VERTEX,"E168");
            var Q13;
            Q13=makeQuery(id+"F1.opExtrude","SWEPT_BODY",BODY,{"disambiguationData":[OSD([sQuery(id+"F0.wireOp",EDGE,"E0.bottom"),sQuery(id+"F0.wireOp",EDGE,"E0.top"),sQuery(id+"F0.wireOp",EDGE,"E0.left"),sQuery(id+"F0.wireOp",EDGE,"E0.right")])]});
            hole(context, id + "F7", {"style" : HoleStyle.SIMPLE, "endStyle" : HoleEndStyle.BLIND, "holeDiameter" : 3 * mm, "holeDepth" : 1 * mm, "tappedDepth" : 12 * mm, "tapClearance" : 3, "locations" : qUnion([Q0, Q1, Q2, Q3, Q4, Q5, Q6, Q7, Q8, Q9, Q10, Q11, Q12]), "scope" : qUnion([Q13])});
        }
        {
            var Q0;
            Q0=makeQuery(id+"F1.opExtrude","SWEPT_FACE",FACE,{"disambiguationData":[OSD([sQuery(id+"F0.wireOp",EDGE,"E0.top")])]});
            cPlane(context, id + "F8", {"entities" : qUnion([Q0]), "cplaneType" : CPlaneType.OFFSET, "offset" : 0 * mm, "width" : 150 * mm, "height" : 150 * mm});
        }
        {
            var Q0;
            Q0=qCreatedBy(id+"F8.planeOp",FACE);
            var sketch = newSketch(context, id + "F9", { "sketchPlane" : qUnion([Q0])});
            skLineSegment(sketch, "E171", {"start": v(-0.67, 2.04) * mm, "end": v(-0.67, -38.18) * mm, "construction": true});
            skPoint(sketch, "E172", {"position": v(29.33, -30) * mm});
            skPoint(sketch, "E173.1.0.0", {"position": v(24.33, -30) * mm});
            skPoint(sketch, "E173.2.0.0", {"position": v(19.33, -30) * mm});
            skPoint(sketch, "E173.3.0.0", {"position": v(14.33, -30) * mm});
            skPoint(sketch, "E173.4.0.0", {"position": v(9.33, -30) * mm});
            skPoint(sketch, "E173.5.0.0", {"position": v(4.33, -30) * mm});
            skPoint(sketch, "E173.6.0.0", {"position": v(-0.67, -30) * mm});
            skPoint(sketch, "E173.7.0.0", {"position": v(-5.67, -30) * mm});
            skPoint(sketch, "E173.8.0.0", {"position": v(-10.67, -30) * mm});
            skPoint(sketch, "E173.9.0.0", {"position": v(-15.67, -30) * mm});
            skPoint(sketch, "E173.10.0.0", {"position": v(-20.67, -30) * mm});
            skPoint(sketch, "E173.11.0.0", {"position": v(-25.67, -30) * mm});
            skPoint(sketch, "E173.12.0.0", {"position": v(-30.67, -30) * mm});
            skLineSegment(sketch, "E173.direction1", {"start": v(29.33, -30) * mm, "end": v(24.33, -30) * mm, "construction": true});
            skSolve(sketch);
        }
        {
            var Q0;
            Q0=sQuery(id+"F9.wireOp",VERTEX,"E173.1.0.0");
            var Q1;
            Q1=sQuery(id+"F9.wireOp",VERTEX,"E172");
            var Q2;
            Q2=sQuery(id+"F9.wireOp",VERTEX,"E173.2.0.0");
            var Q3;
            Q3=sQuery(id+"F9.wireOp",VERTEX,"E173.4.0.0");
            var Q4;
            Q4=sQuery(id+"F9.wireOp",VERTEX,"E173.3.0.0");
            var Q5;
            Q5=sQuery(id+"F9.wireOp",VERTEX,"E173.6.0.0");
            var Q6;
            Q6=sQuery(id+"F9.wireOp",VERTEX,"E173.5.0.0");
            var Q7;
            Q7=sQuery(id+"F9.wireOp",VERTEX,"E173.8.0.0");
            var Q8;
            Q8=sQuery(id+"F9.wireOp",VERTEX,"E173.10.0.0");
            var Q9;
            Q9=sQuery(id+"F9.wireOp",VERTEX,"E173.7.0.0");
            var Q10;
            Q10=sQuery(id+"F9.wireOp",VERTEX,"E173.9.0.0");
            var Q11;
            Q11=sQuery(id+"F9.wireOp",VERTEX,"E173.12.0.0");
            var Q12;
            Q12=sQuery(id+"F9.wireOp",VERTEX,"E173.11.0.0");
            var Q13;
            Q13=makeQuery(id+"F1.opExtrude","SWEPT_BODY",BODY,{"disambiguationData":[OSD([sQuery(id+"F0.wireOp",EDGE,"E0.bottom"),sQuery(id+"F0.wireOp",EDGE,"E0.top"),sQuery(id+"F0.wireOp",EDGE,"E0.left"),sQuery(id+"F0.wireOp",EDGE,"E0.right")])]});
            hole(context, id + "F10", {"style" : HoleStyle.SIMPLE, "endStyle" : HoleEndStyle.BLIND, "holeDiameter" : 3 * mm, "holeDepth" : 1 * mm, "tappedDepth" : 12 * mm, "tapClearance" : 3, "locations" : qUnion([Q0, Q1, Q2, Q3, Q4, Q5, Q6, Q7, Q8, Q9, Q10, Q11, Q12]), "scope" : qUnion([Q13])});
        }
        {
            var Q0;
            Q0=qCreatedBy(id+"F5.planeOp",FACE);
            var sketch = newSketch(context, id + "F11", { "sketchPlane" : qUnion([Q0])});
            skLineSegment(sketch, "E174", {"start": v(-2.7, 0) * mm, "end": v(37.52, 0) * mm, "construction": true});
            skPoint(sketch, "E175", {"position": v(30, 29.32) * mm});
            skPoint(sketch, "E176.1.0.0", {"position": v(30, 24.32) * mm});
            skPoint(sketch, "E176.2.0.0", {"position": v(30, 19.32) * mm});
            skPoint(sketch, "E176.3.0.0", {"position": v(30, 14.32) * mm});
            skPoint(sketch, "E176.4.0.0", {"position": v(30, 9.32) * mm});
            skPoint(sketch, "E176.5.0.0", {"position": v(30, 4.32) * mm});
            skPoint(sketch, "E176.6.0.0", {"position": v(30, -0.68) * mm});
            skPoint(sketch, "E176.7.0.0", {"position": v(30, -5.68) * mm});
            skPoint(sketch, "E176.8.0.0", {"position": v(30, -10.68) * mm});
            skPoint(sketch, "E176.9.0.0", {"position": v(30, -15.68) * mm});
            skPoint(sketch, "E176.10.0.0", {"position": v(30, -20.67) * mm});
            skPoint(sketch, "E176.11.0.0", {"position": v(30, -25.68) * mm});
            skPoint(sketch, "E176.12.0.0", {"position": v(30, -30.68) * mm});
            skLineSegment(sketch, "E176.direction1", {"start": v(30, 29.32) * mm, "end": v(30, 24.32) * mm, "construction": true});
            skPoint(sketch, "E177", {"position": v(0, 0) * mm});
            skSolve(sketch);
        }
        {
            var Q0;
            Q0=sQuery(id+"F11.wireOp",VERTEX,"E175");
            var Q1;
            Q1=sQuery(id+"F11.wireOp",VERTEX,"E176.1.0.0");
            var Q2;
            Q2=sQuery(id+"F11.wireOp",VERTEX,"E176.3.0.0");
            var Q3;
            Q3=sQuery(id+"F11.wireOp",VERTEX,"E176.2.0.0");
            var Q4;
            Q4=sQuery(id+"F11.wireOp",VERTEX,"E176.4.0.0");
            var Q5;
            Q5=sQuery(id+"F11.wireOp",VERTEX,"E176.5.0.0");
            var Q6;
            Q6=sQuery(id+"F11.wireOp",VERTEX,"E176.6.0.0");
            var Q7;
            Q7=sQuery(id+"F11.wireOp",VERTEX,"E176.7.0.0");
            var Q8;
            Q8=sQuery(id+"F11.wireOp",VERTEX,"E176.10.0.0");
            var Q9;
            Q9=sQuery(id+"F11.wireOp",VERTEX,"E176.9.0.0");
            var Q10;
            Q10=sQuery(id+"F11.wireOp",VERTEX,"E176.11.0.0");
            var Q11;
            Q11=sQuery(id+"F11.wireOp",VERTEX,"E176.8.0.0");
            var Q12;
            Q12=sQuery(id+"F11.wireOp",VERTEX,"E176.12.0.0");
            var Q13;
            Q13=makeQuery(id+"F1.opExtrude","SWEPT_BODY",BODY,{"disambiguationData":[OSD([sQuery(id+"F0.wireOp",EDGE,"E0.bottom"),sQuery(id+"F0.wireOp",EDGE,"E0.top"),sQuery(id+"F0.wireOp",EDGE,"E0.left"),sQuery(id+"F0.wireOp",EDGE,"E0.right")])]});
            hole(context, id + "F12", {"style" : HoleStyle.SIMPLE, "endStyle" : HoleEndStyle.THROUGH, "holeDiameter" : 3 * mm, "tappedDepth" : 12 * mm, "tapClearance" : 3, "locations" : qUnion([Q0, Q1, Q2, Q3, Q4, Q5, Q6, Q7, Q8, Q9, Q10, Q11, Q12]), "scope" : qUnion([Q13])});
        }
        {
            var Q0;
            Q0=makeQuery(id+"F1.opExtrude","SWEPT_FACE",FACE,{"disambiguationData":[OSD([sQuery(id+"F0.wireOp",EDGE,"E0.bottom")])]});
            cPlane(context, id + "F13", {"entities" : qUnion([Q0]), "cplaneType" : CPlaneType.OFFSET, "offset" : 0 * mm, "width" : 150 * mm, "height" : 150 * mm});
        }
        {
            var Q0;
            Q0=qCreatedBy(id+"F13.planeOp",FACE);
            var sketch = newSketch(context, id + "F14", { "sketchPlane" : qUnion([Q0])});
            skLineSegment(sketch, "E178", {"start": v(0, -8) * mm, "end": v(0, 32.22) * mm, "construction": true});
            skPoint(sketch, "E179", {"position": v(-30, 30) * mm});
            skPoint(sketch, "E180.1.0.0", {"position": v(-25, 30) * mm});
            skPoint(sketch, "E180.2.0.0", {"position": v(-20, 30) * mm});
            skPoint(sketch, "E180.3.0.0", {"position": v(-15, 30) * mm});
            skPoint(sketch, "E180.4.0.0", {"position": v(-10, 30) * mm});
            skPoint(sketch, "E180.5.0.0", {"position": v(-5, 30) * mm});
            skPoint(sketch, "E180.6.0.0", {"position": v(0, 30) * mm});
            skPoint(sketch, "E180.7.0.0", {"position": v(5, 30) * mm});
            skPoint(sketch, "E180.8.0.0", {"position": v(10, 30) * mm});
            skPoint(sketch, "E180.9.0.0", {"position": v(15, 30) * mm});
            skPoint(sketch, "E180.10.0.0", {"position": v(20, 30) * mm});
            skPoint(sketch, "E180.11.0.0", {"position": v(25, 30) * mm});
            skPoint(sketch, "E180.12.0.0", {"position": v(30, 30) * mm});
            skLineSegment(sketch, "E180.direction1", {"start": v(-30, 30) * mm, "end": v(-25, 30) * mm, "construction": true});
            skPoint(sketch, "E181", {"position": v(0, 0) * mm});
            skSolve(sketch);
        }
        {
            var Q0;
            Q0=sQuery(id+"F14.wireOp",VERTEX,"E180.12.0.0");
            var Q1;
            Q1=sQuery(id+"F14.wireOp",VERTEX,"E180.10.0.0");
            var Q2;
            Q2=sQuery(id+"F14.wireOp",VERTEX,"E180.8.0.0");
            var Q3;
            Q3=sQuery(id+"F14.wireOp",VERTEX,"E180.11.0.0");
            var Q4;
            Q4=sQuery(id+"F14.wireOp",VERTEX,"E180.6.0.0");
            var Q5;
            Q5=sQuery(id+"F14.wireOp",VERTEX,"E180.9.0.0");
            var Q6;
            Q6=sQuery(id+"F14.wireOp",VERTEX,"E180.7.0.0");
            var Q7;
            Q7=sQuery(id+"F14.wireOp",VERTEX,"E180.4.0.0");
            var Q8;
            Q8=sQuery(id+"F14.wireOp",VERTEX,"E180.5.0.0");
            var Q9;
            Q9=sQuery(id+"F14.wireOp",VERTEX,"E180.3.0.0");
            var Q10;
            Q10=sQuery(id+"F14.wireOp",VERTEX,"E180.1.0.0");
            var Q11;
            Q11=sQuery(id+"F14.wireOp",VERTEX,"E180.2.0.0");
            var Q12;
            Q12=sQuery(id+"F14.wireOp",VERTEX,"E179");
            var Q13;
            Q13=makeQuery(id+"F1.opExtrude","SWEPT_BODY",BODY,{"disambiguationData":[OSD([sQuery(id+"F0.wireOp",EDGE,"E0.bottom"),sQuery(id+"F0.wireOp",EDGE,"E0.top"),sQuery(id+"F0.wireOp",EDGE,"E0.left"),sQuery(id+"F0.wireOp",EDGE,"E0.right")])]});
            hole(context, id + "F15", {"style" : HoleStyle.SIMPLE, "endStyle" : HoleEndStyle.THROUGH, "holeDiameter" : 3 * mm, "tappedDepth" : 12 * mm, "tapClearance" : 3, "locations" : qUnion([Q0, Q1, Q2, Q3, Q4, Q5, Q6, Q7, Q8, Q9, Q10, Q11, Q12]), "scope" : qUnion([Q13])});
        }
        {
            var Q0;
            Q0=makeQuery(id+"F1.opExtrude","SWEPT_BODY",BODY,{"disambiguationData":[OSD([sQuery(id+"F0.wireOp",EDGE,"E0.bottom"),sQuery(id+"F0.wireOp",EDGE,"E0.top"),sQuery(id+"F0.wireOp",EDGE,"E0.left"),sQuery(id+"F0.wireOp",EDGE,"E0.right")])]});
            transform(context, id + "F16", {"entities" : qUnion([Q0]), "transformType" : TransformType.TRANSLATION_3D, "dx" : 0 * mm, "dy" : 0 * mm, "dz" : 0 * mm, "makeCopy" : true});
        }
        {
            var Q0;
            Q0=makeQuery(id+"F16.opPattern","COPY",BODY,{"derivedFrom":makeQuery(id+"F1.opExtrude","SWEPT_BODY",BODY,{"disambiguationData":[OSD([sQuery(id+"F0.wireOp",EDGE,"E0.bottom"),sQuery(id+"F0.wireOp",EDGE,"E0.top"),sQuery(id+"F0.wireOp",EDGE,"E0.left"),sQuery(id+"F0.wireOp",EDGE,"E0.right")])]}),"instanceName":"1"});
            deleteBodies(context, id + "F17", {"entities" : qUnion([Q0])});
        }
    });
